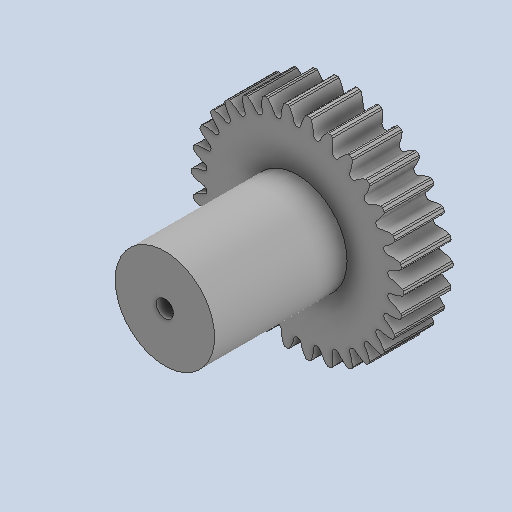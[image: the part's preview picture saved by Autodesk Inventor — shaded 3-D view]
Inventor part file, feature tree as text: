
AUTODESK INVENTOR PART (.ipt)
format: ipt  version: 2024 (Build 280153000, 153)  size: 746,496 bytes
history: native  units: mm
features: extrude x4, pattern_circular x2, fillet x1, sketch x1, other x1
ambient origin geometry x8: Origin, YZ Plane, XZ Plane, XY Plane, X Axis, Y Axis, Z Axis, Center Point
bodies: Solid1 (feature_tree)
feature tree (9):
  extrude  "Extrusion1"  TaperAngle=0.0deg  [1 undecoded]
  extrude  "Extrusion2"  Depth=300.0mm TaperAngle=360.0deg
  pattern_circular  "Circular Pattern1"  Count=3  [1 undecoded]
  extrude  "Extrusion3"  Depth=5.2mm
  fillet  "Fillet1"  Radius=40.0mm
  pattern_circular  "Circular Pattern2"  [2 undecoded]
  sketch  "Sketch2"  dims[d0=15.0mm d1=0.0mm d2=0.0mm d3=0.0mm d4=300.0mm d5=360.0deg d7=30.0mm d8=5.2mm d9=40.0mm d10=0.0mm d11=0.5mm d12=300.0mm d13=360.0deg d15=0.0mm d16=0.0mm d14=0.0mm]
  other  "Srf1"
  extrude  "ExtrusionSrf1"  Depth=300.0mm TaperAngle=360.0deg
note: 4 required parameter values undecoded (feature->parameter linkage not recoverable at this tier; creation-order binding heuristic only, values carry confidence <= 0.55)
